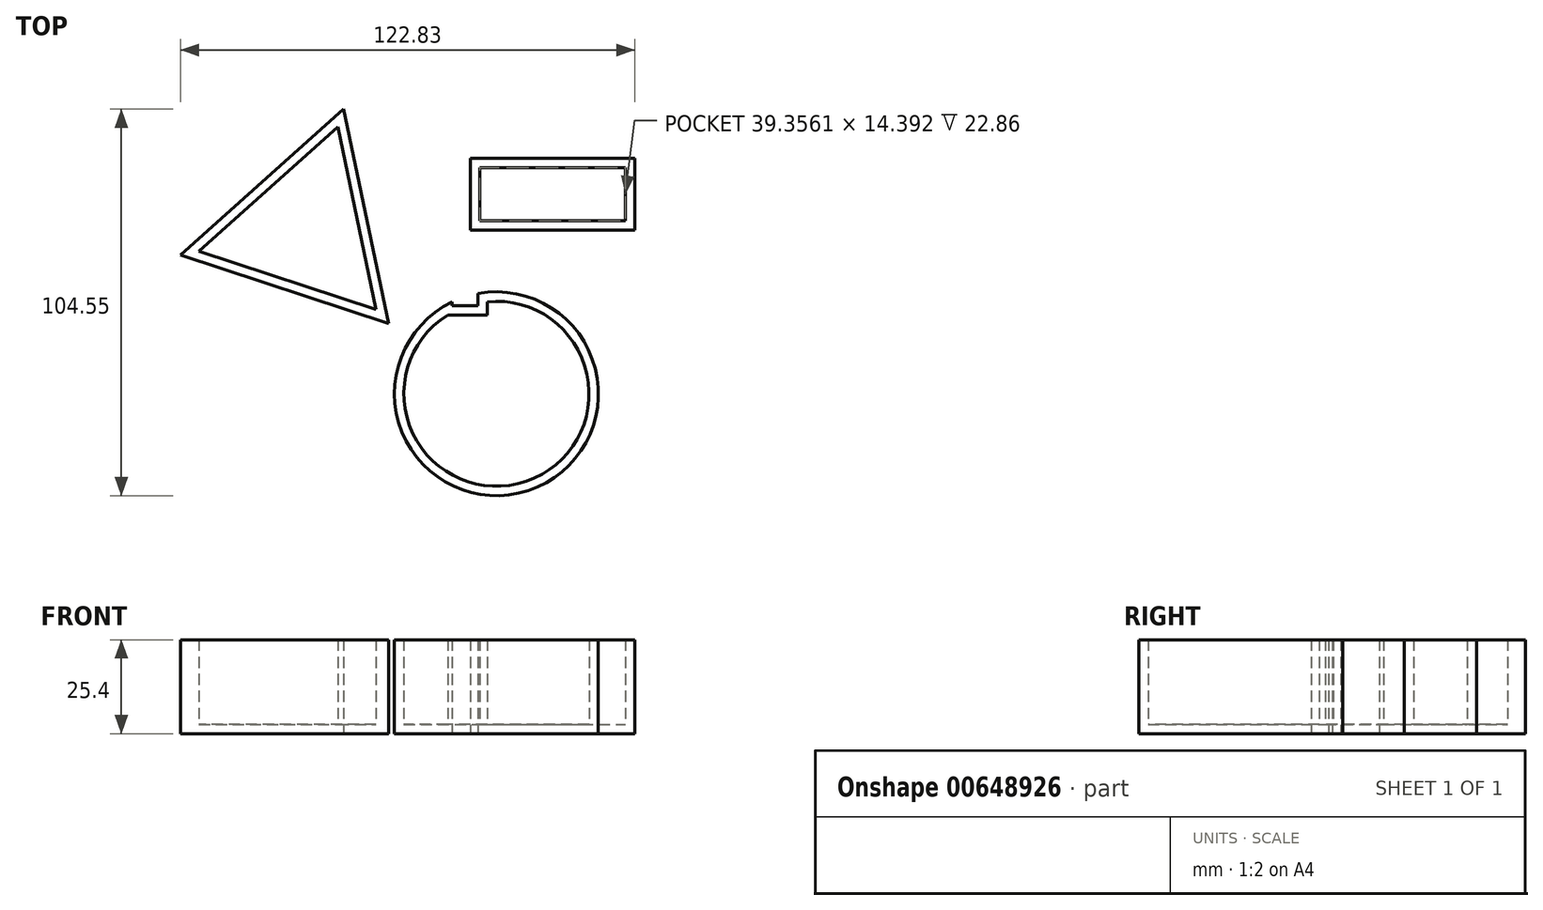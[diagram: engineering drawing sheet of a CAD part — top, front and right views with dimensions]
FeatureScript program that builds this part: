
annotation { "Feature Type Name" : "Feature", "Feature Type Description" : "" }
export const myFeature = defineFeature(function(context is Context, id is Id, definition is map)
    precondition{}
    {
        {
            var Q0;
            Q0=qCreatedBy(makeId("Top.planeOp"),FACE);
            var sketch = newSketch(context, id + "F0", { "sketchPlane" : qUnion([Q0])});
            skLineSegment(sketch, "E0.bottom", {"start": v(5.62, -3) * mm, "end": v(-1.37, -3) * mm});
            skLineSegment(sketch, "E0.top", {"start": v(5.62, 3) * mm, "end": v(-1.37, 3) * mm});
            skLineSegment(sketch, "E0.left", {"start": v(5.62, -3) * mm, "end": v(5.62, 3) * mm});
            skLineSegment(sketch, "E0.right", {"start": v(-1.37, -3) * mm, "end": v(-1.37, 3) * mm});
            skPoint(sketch, "E0.middle", {"position": v(2.12, 0) * mm});
            skLineSegment(sketch, "E1.bottom", {"start": v(3.62, 17.47) * mm, "end": v(48.06, 17.47) * mm});
            skLineSegment(sketch, "E1.top", {"start": v(3.62, 36.95) * mm, "end": v(48.06, 36.95) * mm});
            skLineSegment(sketch, "E1.left", {"start": v(3.62, 17.47) * mm, "end": v(3.62, 36.95) * mm});
            skLineSegment(sketch, "E1.right", {"start": v(48.06, 17.47) * mm, "end": v(48.06, 36.95) * mm});
            skPoint(sketch, "E1.middle", {"position": v(25.84, 27.21) * mm});
            skCircle(sketch, "E2.cCircle", {"center": v(-41.32, 17.72) * mm, "radius": 17.09 * mm, "construction": true});
            skLineSegment(sketch, "E2.0", {"start": v(-30.64, 50.19) * mm, "end": v(-18.54, -7.75) * mm});
            skLineSegment(sketch, "E2.1", {"start": v(-18.54, -7.75) * mm, "end": v(-74.77, 10.73) * mm});
            skLineSegment(sketch, "E2.2", {"start": v(-74.77, 10.73) * mm, "end": v(-30.64, 50.19) * mm});
            skPoint(sketch, "E2.0.midPoint", {"position": v(-24.59, 21.22) * mm});
            skCircle(sketch, "E3", {"center": v(10.65, -26.8) * mm, "radius": 27.57 * mm});
            skSolve(sketch);
        }
        {
            var Q0;
            {var subQ0=sQuery(id+"F0.wireOp",EDGE,"E0.bottom");Q0=makeQuery(id+"F0.imprint","IMPRINT",FACE,{"disambiguationData":[TD([[makeQuery(id+"F0.imprint","IMPRINT",EDGE,{"derivedFrom":subQ0}),1.0]])]});}
            var Q1;
            Q1=makeQuery(id+"F0.imprint","IMPRINT",FACE,{"disambiguationData":[TD([[makeQuery(id+"F0.imprint","IMPRINT",EDGE,{"derivedFrom":sQuery(id+"F0.wireOp",EDGE,"E2.0")}),-1.0]])]});
            var Q2;
            Q2=makeQuery(id+"F0.imprint","IMPRINT",FACE,{"disambiguationData":[TD([[makeQuery(id+"F0.imprint","IMPRINT",EDGE,{"derivedFrom":sQuery(id+"F0.wireOp",EDGE,"E1.bottom")}),1.0]])]});
            extrude(context, id + "F1", {"entities" : qUnion([Q0, Q1, Q2]), "depth" : 25.4 * mm, "offsetDistance" : 25.4 * mm});
        }
        {
            var Q0;
            Q0=makeQuery(id+"F1.opExtrude","CAP_FACE",FACE,{"disambiguationData":[OSD([sQuery(id+"F0.wireOp",EDGE,"E2.0"),sQuery(id+"F0.wireOp",EDGE,"E2.1"),sQuery(id+"F0.wireOp",EDGE,"E2.2")])],"isStart":false});
            var Q1;
            Q1=makeQuery(id+"F1.opExtrude","CAP_FACE",FACE,{"disambiguationData":[OSD([sQuery(id+"F0.wireOp",EDGE,"E0.bottom"),sQuery(id+"F0.wireOp",EDGE,"E0.left"),sQuery(id+"F0.wireOp",EDGE,"E0.right"),sQuery(id+"F0.wireOp",EDGE,"E3")])],"isStart":false});
            var Q2;
            Q2=makeQuery(id+"F1.opExtrude","CAP_FACE",FACE,{"disambiguationData":[OSD([sQuery(id+"F0.wireOp",EDGE,"E1.bottom"),sQuery(id+"F0.wireOp",EDGE,"E1.top"),sQuery(id+"F0.wireOp",EDGE,"E1.left"),sQuery(id+"F0.wireOp",EDGE,"E1.right")])],"isStart":false});
            shell(context, id + "F2", {"entities" : qUnion([Q0, Q1, Q2]), "thickness" : 2.54 * mm});
        }
    });
